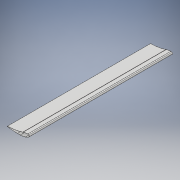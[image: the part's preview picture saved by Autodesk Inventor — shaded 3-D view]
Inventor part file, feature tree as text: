
AUTODESK INVENTOR PART (.ipt)
format: ipt  version: 2018.2 (Build 222227000, 227)  size: 128,000 bytes
history: native  units: mm
features: extrude x1, shell x1, sketch x1, projected_geometry x1
ambient origin geometry x8: Origin, YZ Plane, XZ Plane, XY Plane, X Axis, Y Axis, Z Axis, Center Point
bodies: Body1 (feature_tree)
feature tree (4):
  extrude  "押し出し1"  Depth=946.0mm TaperAngle=0.0deg
  shell  "シェル1"  Thickness=1.0mm
  sketch  "スケッチ1"
  projected_geometry  "投影ループ1"
